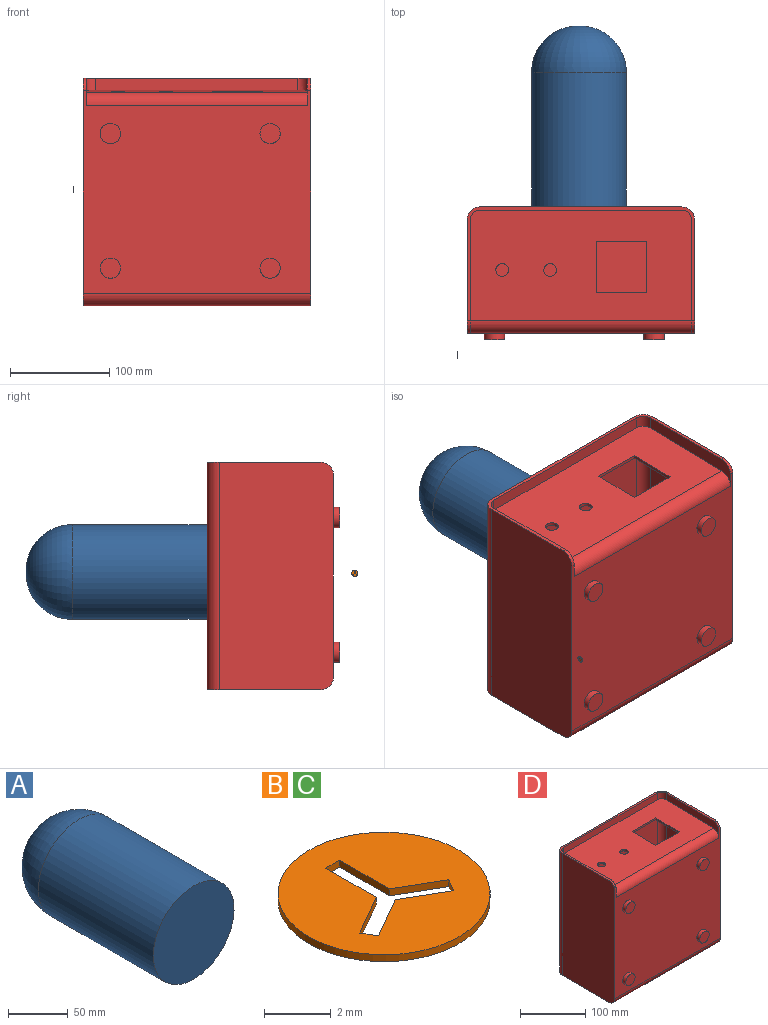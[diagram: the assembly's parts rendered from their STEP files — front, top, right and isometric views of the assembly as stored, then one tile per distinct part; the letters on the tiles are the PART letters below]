
ASSEMBLY  parts=4 mates=3
PART A: 3 faces, bbox 95.3x183.2x95.3 mm
  f0: cylinder r=47.62mm len=135.59mm, axis (0,1,0), area 40574mm2, adj f1,f2
  f1: plane 95.25x95.25mm, normal (0,-1,0), area 7125.6mm2, adj f0
  f2: torus R=1.11mm, axis (0,1,0), area 14108.3mm2, adj f0
PART B: 12 faces, bbox 6.4x6.4x0.3 mm
  f0: plane 2.11x0.25mm, normal (-1,0,0), area 0.5mm2, adj f1,f9,f10,f11
  f1: plane 1.59x0.92mm, normal (-0.5,-0.87,0), area 0.5mm2, adj f0,f2,f10,f11
  f2: plane 0.51x0.29mm, normal (-0.87,0.5,0), area 0.1mm2, adj f1,f3,f10,f11
  f3: plane 1.57x0.91mm, normal (0.5,0.87,0), area 0.5mm2, adj f2,f4,f10,f11
  f4: plane 1.69x0.97mm, normal (-0.5,0.87,0), area 0.5mm2, adj f3,f5,f10,f11
  f5: plane 0.51x0.29mm, normal (0.87,0.5,0), area 0.1mm2, adj f4,f6,f10,f11
  f6: plane 1.66x0.96mm, normal (0.5,-0.87,0), area 0.5mm2, adj f5,f7,f10,f11
  f7: plane 2.14x0.25mm, normal (1,0,0), area 0.5mm2, adj f6,f9,f10,f11
  f8: cylinder r=3.17mm len=6.35mm, axis (0,0,-1), area 5.1mm2, adj f10,f11
  f9: plane 0.59x0.25mm, normal (0,-1,0), area 0.1mm2, adj f0,f7,f10,f11
  f10: plane 6.35x6.35mm, normal (0,0,1), area 28.1mm2, adj f0,f1,f2,f3,f4,f5,f6,f7
  f11: plane 6.35x6.35mm, normal (0,0,-1), area 28.1mm2, adj f0,f1,f2,f3,f4,f5,f6,f7
PART C: same geometry as B
PART D: 62 faces, bbox 228.7x133.4x228.7 mm
  f0: plane 213.26x203.2mm, normal (0,-1,0), area 43333.8mm2, adj f1,f2,f4,f7
  f1: cylinder r=9.53mm len=213.26mm, axis (0,0,-1), area 3189.3mm2, adj f0,f4,f7,f13,f25
  f2: cylinder r=9.53mm len=213.26mm, axis (0,0,-1), area 3189.7mm2, adj f0,f4,f7,f12,f25
  f3: plane 222.33x111.45mm, normal (0,-0.02,1), area 21884.2mm2, adj f8,f9,f14,f15,f16,f26,f48,f49
  f4: plane 222.33x111.39mm, normal (0,0.02,-1), area 21870.4mm2, adj f0,f1,f2,f12,f13,f22,f48,f49
  f5: plane 228.6x114.3mm, normal (-1,0,0), area 26059.8mm2, adj f7,f10,f11,f19,f24,f28
  f6: plane 228.6x114.3mm, normal (1,0,0), area 26059.8mm2, adj f7,f10,f11,f17,f24,f27
  f7: plane 228.6x114.3mm, normal (0,0,-1), area 23338.4mm2, adj f0,f1,f2,f5,f6,f17,f18,f19
  f8: plane 114.3x27.03mm, normal (1,0,0), area 1537.4mm2, adj f3,f10,f11,f14,f26,f28
  f9: plane 114.3x27.03mm, normal (-1,0,0), area 1537.4mm2, adj f3,f10,f11,f16,f26,f27
  f10: plane 228.6x203.2mm, normal (0,-1,0), area 41965.5mm2, adj f5,f6,f8,f9,f24,f26,f27,f28
  f11: plane 228.6x114.3mm, normal (0,0,1), area 1401.2mm2, adj f5,f6,f8,f9,f14,f15,f16,f17
  f12: plane 209.9x111.13mm, normal (-1,0,0), area 23166.6mm2, adj f2,f4,f20,f21,f22,f23
  f13: plane 209.9x111.13mm, normal (1,0,0), area 23166.6mm2, adj f1,f4,f20,f21,f22,f23
  f14: cylinder r=9.53mm len=12.35mm, axis (0,0,-1), area 183.4mm2, adj f3,f8,f11,f15
  f15: plane 203.2x12.17mm, normal (0,-1,0), area 2472.4mm2, adj f3,f11,f14,f16
  f16: cylinder r=9.53mm len=12.35mm, axis (0,0,-1), area 183.4mm2, adj f3,f9,f11,f15
  f17: cylinder r=12.7mm len=228.6mm, axis (0,0,-1), area 4560.4mm2, adj f6,f7,f11,f18
  f18: plane 228.6x203.2mm, normal (0,1,0), area 46451.5mm2, adj f7,f11,f17,f19
  f19: cylinder r=12.7mm len=228.6mm, axis (0,0,-1), area 4560.4mm2, adj f5,f7,f11,f18
  f20: cylinder r=9.53mm len=222.25mm, axis (1,0,0), area 3325.3mm2, adj f12,f13,f21,f23
  f21: plane 222.25x188.87mm, normal (0,1,0), area 41976mm2, adj f12,f13,f20,f22
  f22: cylinder r=9.53mm len=222.25mm, axis (1,0,0), area 3284.1mm2, adj f4,f12,f13,f21
  f23: plane 222.25x101.6mm, normal (0,0,1), area 21937.3mm2, adj f12,f13,f20,f25,f29,f30,f31,f32
  f24: cylinder r=12.7mm len=228.6mm, axis (1,0,0), area 4560.4mm2, adj f5,f6,f7,f10
  f25: plane 222.25x3.18mm, normal (0,1,0), area 705.6mm2, adj f1,f2,f7,f23
  f26: cylinder r=12.7mm len=222.25mm, axis (1,0,0), area 4378.8mm2, adj f3,f8,f9,f10
  f27: cylinder r=12.7mm len=12.7mm, axis (1,0,0), area 63.3mm2, adj f6,f9,f10,f11
  f28: cylinder r=12.7mm len=12.7mm, axis (1,0,0), area 63.3mm2, adj f5,f8,f10,f11
  f29: cylinder r=3.28mm len=6.57mm, axis (0,0,-1), area 65.5mm2, adj f7,f23
  f30: cylinder r=3.28mm len=6.57mm, axis (0,0,-1), area 65.5mm2, adj f7,f23
  f31: cylinder r=3.28mm len=6.57mm, axis (0,0,-1), area 65.5mm2, adj f7,f23
  f32: cylinder r=3.28mm len=6.57mm, axis (0,0,-1), area 65.5mm2, adj f7,f23
  f33: cylinder r=3.28mm len=6.57mm, axis (0,0,-1), area 65.5mm2, adj f7,f23
  f34: cylinder r=3.28mm len=6.57mm, axis (0,0,-1), area 65.5mm2, adj f7,f23
  f35: cylinder r=3.28mm len=6.57mm, axis (0,0,-1), area 65.5mm2, adj f7,f23
  f36: cylinder r=3.28mm len=6.57mm, axis (0,0,-1), area 65.5mm2, adj f7,f23
  f37: cylinder r=3.28mm len=6.57mm, axis (0,0,-1), area 65.5mm2, adj f7,f23
  f38: cylinder r=3.28mm len=6.57mm, axis (0,0,-1), area 65.5mm2, adj f7,f23
  f39: cylinder r=3.28mm len=6.57mm, axis (0,0,-1), area 65.5mm2, adj f7,f23
  f40: cylinder r=3.28mm len=6.57mm, axis (0,0,-1), area 65.5mm2, adj f7,f23
  f41: cylinder r=3.28mm len=6.57mm, axis (0,0,-1), area 65.5mm2, adj f7,f23
  f42: cylinder r=3.28mm len=6.57mm, axis (0,0,-1), area 65.5mm2, adj f7,f23
  f43: cylinder r=3.28mm len=6.57mm, axis (0,0,-1), area 65.5mm2, adj f7,f23
  f44: cylinder r=3.28mm len=6.57mm, axis (0,0,-1), area 65.5mm2, adj f7,f23
  f45: cylinder r=3.28mm len=6.57mm, axis (0,0,-1), area 65.5mm2, adj f7,f23
  f46: cylinder r=3.28mm len=6.57mm, axis (0,0,-1), area 65.5mm2, adj f7,f23
  f47: cylinder r=3.28mm len=6.57mm, axis (0,0,-1), area 65.5mm2, adj f7,f23
  f48: cylinder r=6.35mm len=12.76mm, axis (0,-0.02,1), area 126.7mm2, adj f3,f4
  f49: cylinder r=6.35mm len=12.76mm, axis (0,-0.02,1), area 126.7mm2, adj f3,f4
  f50: plane 50.8x3.17mm, normal (0,-1,-0.02), area 161.3mm2, adj f3,f4,f51,f53
  f51: plane 50.85x4.16mm, normal (1,0,0), area 161.3mm2, adj f3,f4,f50,f52
  f52: plane 50.8x3.17mm, normal (0,1,0.02), area 161.3mm2, adj f3,f4,f51,f53
  f53: plane 50.85x4.16mm, normal (-1,0,0), area 161.3mm2, adj f3,f4,f50,f52
  f54: cylinder r=10.17mm len=20.35mm, axis (0,1,0), area 405.9mm2, adj f10,f55
  f55: plane 20.35x20.35mm, normal (0,-1,0), area 325.2mm2, adj f54
  f56: cylinder r=10.17mm len=20.35mm, axis (0,1,0), area 405.9mm2, adj f10,f57
  f57: plane 20.35x20.35mm, normal (0,-1,0), area 325.2mm2, adj f56
  f58: cylinder r=10.17mm len=20.35mm, axis (0,1,0), area 405.9mm2, adj f10,f59
  f59: plane 20.35x20.35mm, normal (0,-1,0), area 325.2mm2, adj f58
  f60: cylinder r=10.17mm len=20.35mm, axis (0,1,0), area 405.9mm2, adj f10,f61
  f61: plane 20.35x20.35mm, normal (0,-1,0), area 325.2mm2, adj f60
PLACE A rot(axis=(0,1,0),2deg) t=(143.18,259.95,97.18)mm
PLACE B rot(axis=(0.58,0.58,0.58),120deg) t=(-139.44,58.04,161.39)mm
PLACE C rot(axis=(-1,0.02,0.02),90deg) t=(-21.89,213.72,138.39)mm
PLACE D t=(-25.36,85.55,-15.45)mm
MATE planar C.f10 <-> D.f18  axis (0,1,0) through (-12.71,213.97,197.92)mm
MATE planar A.f0 <-> D.f18  axis (0,-1,0) through (-17.24,213.97,102.85)mm
MATE planar D.f5 <-> D.f18  axis (-1,0,0) through (-129.6,144.26,98.85)mm
